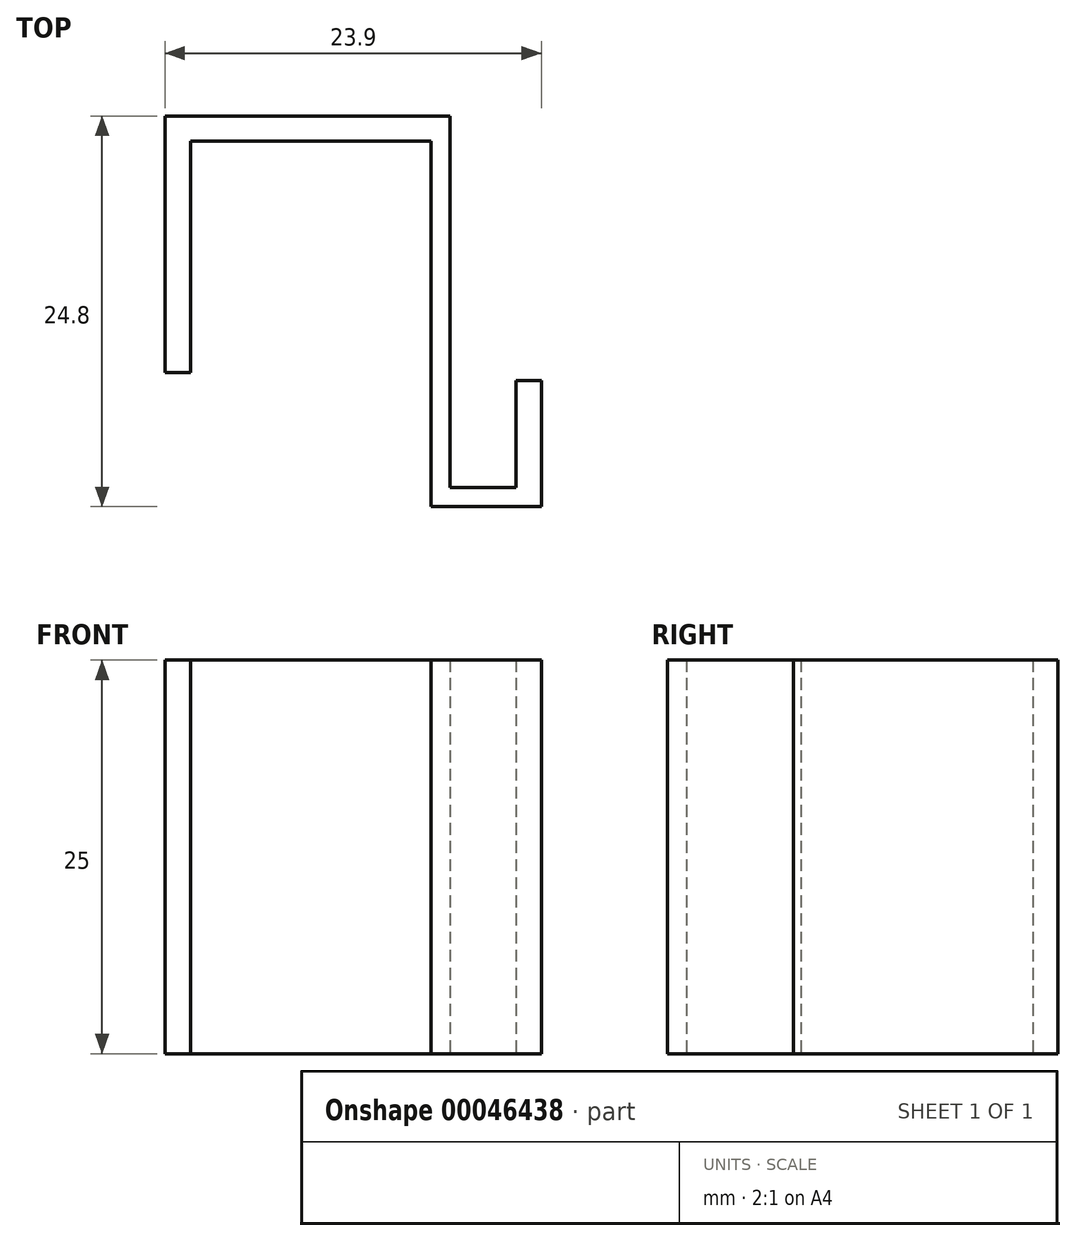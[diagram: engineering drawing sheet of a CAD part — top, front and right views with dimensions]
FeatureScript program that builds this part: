
annotation { "Feature Type Name" : "Feature", "Feature Type Description" : "" }
export const myFeature = defineFeature(function(context is Context, id is Id, definition is map)
    precondition{}
    {
        {
            var Q0;
            Q0=qCreatedBy(makeId("Top.planeOp"),FACE);
            var sketch = newSketch(context, id + "F0", { "sketchPlane" : qUnion([Q0])});
            skLineSegment(sketch, "E0", {"start": v(0, 0) * mm, "end": v(0, 16.3) * mm});
            skLineSegment(sketch, "E1", {"start": v(0, 16.3) * mm, "end": v(18.1, 16.3) * mm});
            skLineSegment(sketch, "E2", {"start": v(18.1, 16.3) * mm, "end": v(18.1, -7.3) * mm});
            skLineSegment(sketch, "E3", {"start": v(18.1, -7.3) * mm, "end": v(22.3, -7.3) * mm});
            skLineSegment(sketch, "E4", {"start": v(22.3, -7.3) * mm, "end": v(22.3, -0.5) * mm});
            skLineSegment(sketch, "E5", {"start": v(22.3, -0.5) * mm, "end": v(23.9, -0.5) * mm});
            skLineSegment(sketch, "E6", {"start": v(23.9, -0.5) * mm, "end": v(23.9, -8.5) * mm});
            skLineSegment(sketch, "E7", {"start": v(23.9, -8.5) * mm, "end": v(16.9, -8.5) * mm});
            skLineSegment(sketch, "E8", {"start": v(16.9, -8.5) * mm, "end": v(16.9, 14.7) * mm});
            skLineSegment(sketch, "E9", {"start": v(16.9, 14.7) * mm, "end": v(1.6, 14.7) * mm});
            skLineSegment(sketch, "E10", {"start": v(1.6, 14.7) * mm, "end": v(1.6, 0) * mm});
            skLineSegment(sketch, "E11", {"start": v(1.6, 0) * mm, "end": v(0, 0) * mm});
            skSolve(sketch);
        }
        {
            var Q0;
            Q0=makeQuery(id+"F0.imprint","IMPRINT",FACE,{"disambiguationData":[TD([[makeQuery(id+"F0.imprint","IMPRINT",EDGE,{"derivedFrom":sQuery(id+"F0.wireOp",EDGE,"E0")}),-1.0]])]});
            extrude(context, id + "F1", {"entities" : qUnion([Q0]), "depth" : 25 * mm});
        }
    });
